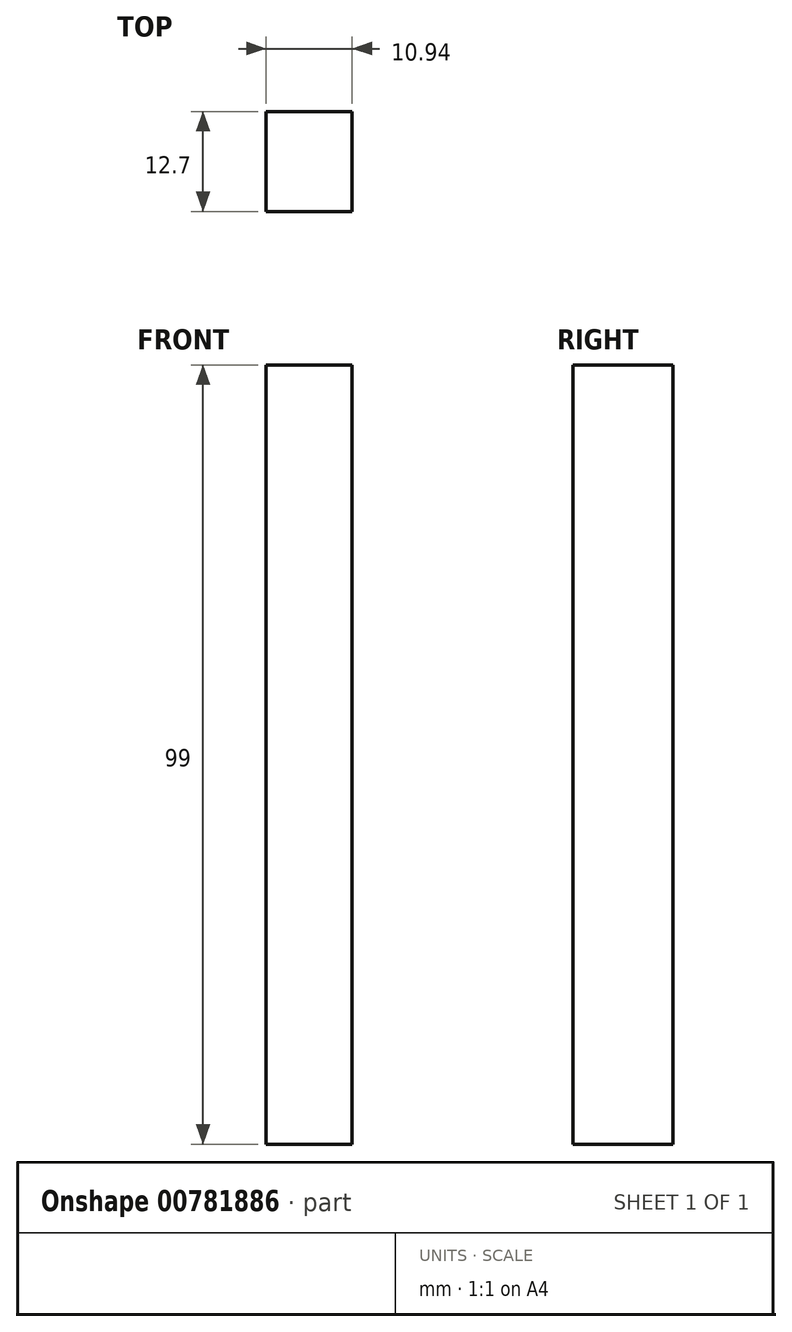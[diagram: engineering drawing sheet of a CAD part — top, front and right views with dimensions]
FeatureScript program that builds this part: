
annotation { "Feature Type Name" : "Feature", "Feature Type Description" : "" }
export const myFeature = defineFeature(function(context is Context, id is Id, definition is map)
    precondition{}
    {
        {
            var Q0;
            Q0=qCreatedBy(makeId("Front.planeOp"),FACE);
            var sketch = newSketch(context, id + "F0", { "sketchPlane" : qUnion([Q0])});
            skLineSegment(sketch, "E0", {"start": v(-6.19, 50.22) * mm, "end": v(-6.19, -48.78) * mm});
            skLineSegment(sketch, "E1", {"start": v(-6.19, -48.78) * mm, "end": v(4.75, -48.78) * mm});
            skLineSegment(sketch, "E2", {"start": v(-6.19, 50.22) * mm, "end": v(4.75, 50.22) * mm});
            skLineSegment(sketch, "E3", {"start": v(4.75, 50.22) * mm, "end": v(4.75, -48.78) * mm});
            skSolve(sketch);
        }
        {
            var Q0;
            Q0=makeQuery(id+"F0.imprint","IMPRINT",FACE,{"disambiguationData":[TD([[makeQuery(id+"F0.imprint","IMPRINT",EDGE,{"derivedFrom":sQuery(id+"F0.wireOp",EDGE,"E0")}),1.0]])]});
            extrude(context, id + "F1", {"entities" : qUnion([Q0]), "depth" : 12.7 * mm, "offsetDistance" : 25.4 * mm});
        }
    });
